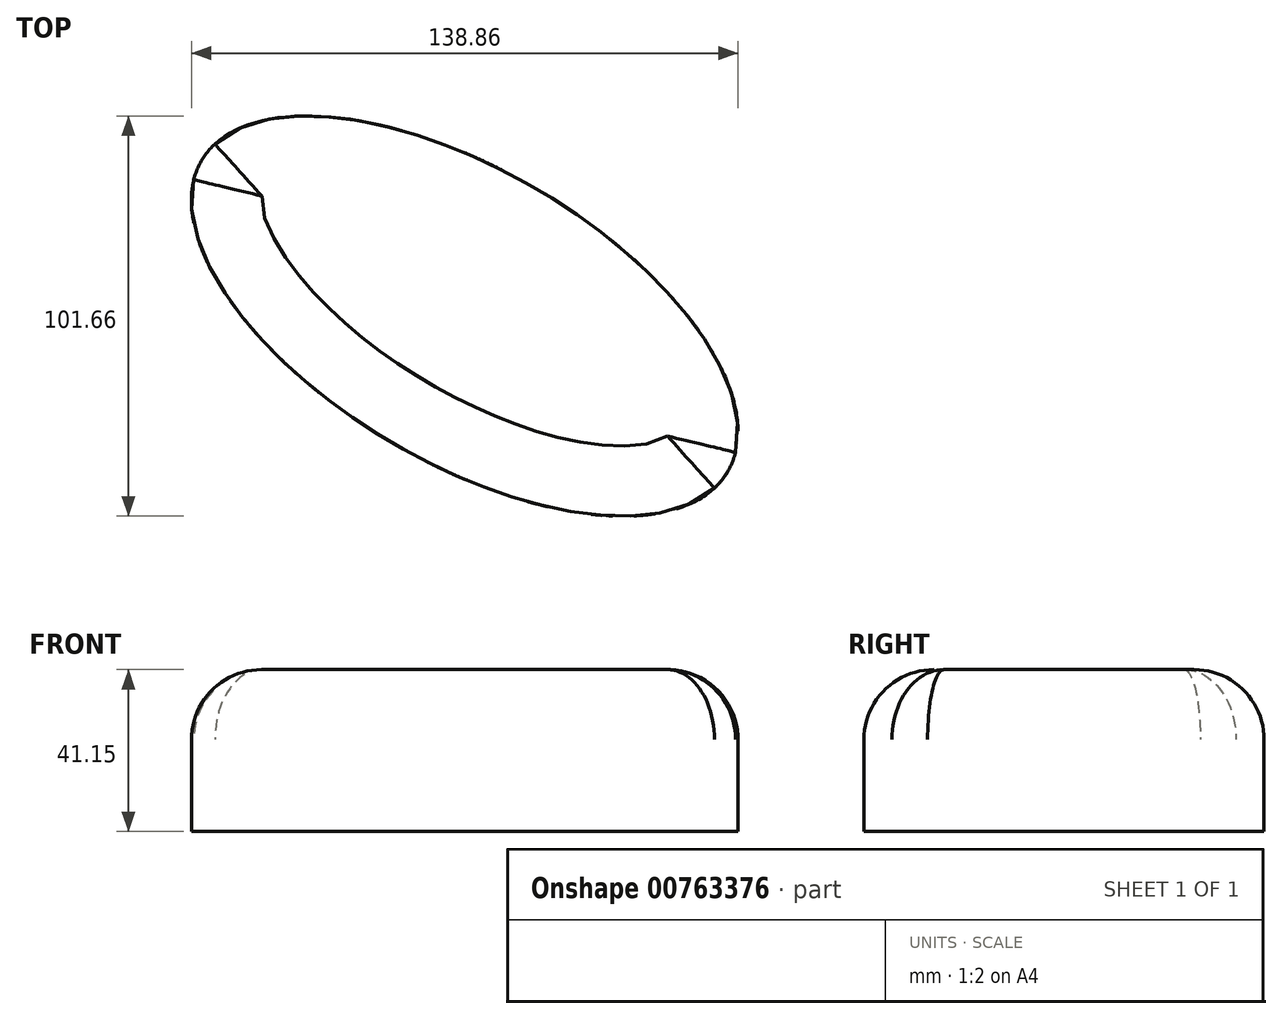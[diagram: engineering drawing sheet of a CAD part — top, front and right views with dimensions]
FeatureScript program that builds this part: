
annotation { "Feature Type Name" : "Feature", "Feature Type Description" : "" }
export const myFeature = defineFeature(function(context is Context, id is Id, definition is map)
    precondition{}
    {
        {
            var Q0;
            Q0=qCreatedBy(makeId("Top.planeOp"),FACE);
            var sketch = newSketch(context, id + "F0", { "sketchPlane" : qUnion([Q0])});
            skEllipse(sketch, "E0", {"center": v(-36.78, 0) * mm, "majorRadius": 77.65 * mm, "minorRadius": 37.09 * mm, "majorAxis": v(0.86, -0.5)});
            skSolve(sketch);
        }
        {
            var Q0;
            Q0 = qSketchRegion(id + "F0", true);
            extrude(context, id + "F1", {"entities" : qUnion([Q0]), "depth" : 41.15 * mm, "offsetDistance" : 25.4 * mm});
        }
        {
            var Q0;
            Q0=makeQuery(id+"F1.opExtrude","CAP_EDGE",EDGE,{"disambiguationData":[OSD([sQuery(id+"F0.wireOp",EDGE,"E0")])],"isStart":false});
            fillet(context, id + "F2", {"entities" : qUnion([Q0]), "radius" : 17.78 * mm, "tangentPropagation" : true, "allowEdgeOverflow" : false});
        }
    });
